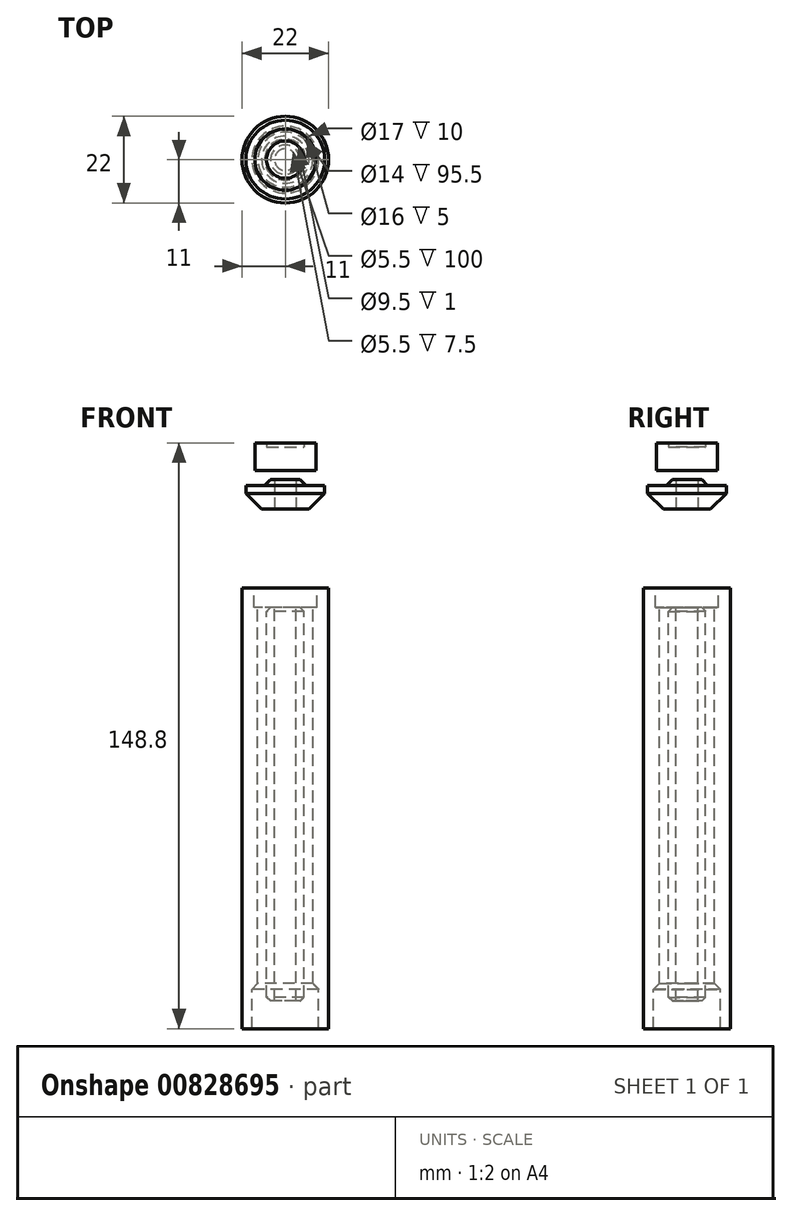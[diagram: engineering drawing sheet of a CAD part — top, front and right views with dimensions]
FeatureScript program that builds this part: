
annotation { "Feature Type Name" : "Feature", "Feature Type Description" : "" }
export const myFeature = defineFeature(function(context is Context, id is Id, definition is map)
    precondition{}
    {
        {
            var Q0;
            Q0=qCreatedBy(makeId("Front.planeOp"),FACE);
            var sketch = newSketch(context, id + "F0", { "sketchPlane" : qUnion([Q0])});
            skLineSegment(sketch, "E0", {"start": v(0, 0) * mm, "end": v(0, 15.44) * mm, "construction": true});
            skLineSegment(sketch, "E1", {"start": v(-2.75, 0) * mm, "end": v(-2.75, 6) * mm});
            skLineSegment(sketch, "E2", {"start": v(-2.75, 6) * mm, "end": v(-10, 6) * mm});
            skLineSegment(sketch, "E3", {"start": v(-10, 6) * mm, "end": v(-10, 4) * mm});
            skLineSegment(sketch, "E4", {"start": v(-10, 4) * mm, "end": v(-6, 0) * mm});
            skLineSegment(sketch, "E5", {"start": v(-6, 0) * mm, "end": v(-2.75, 0) * mm});
            skLineSegment(sketch, "E6.bottom", {"start": v(-2.75, 6) * mm, "end": v(-3.75, 6) * mm});
            skLineSegment(sketch, "E6.top", {"start": v(-2.75, 7.5) * mm, "end": v(-3.75, 7.5) * mm});
            skLineSegment(sketch, "E6.left", {"start": v(-2.75, 6) * mm, "end": v(-2.75, 7.5) * mm});
            skLineSegment(sketch, "E6.right", {"start": v(-3.75, 6) * mm, "end": v(-3.75, 7.5) * mm});
            skSolve(sketch);
        }
        {
            var Q0;
            {var subQ2=sQuery(id+"F0.wireOp",EDGE,"E1");Q0=qUnion([makeQuery(id+"F0.imprint","IMPRINT",FACE,{"disambiguationData":[TD([[makeQuery(id+"F0.imprint","IMPRINT",EDGE,{"derivedFrom":subQ2}),1.0]])]}),makeQuery(id+"F0.imprint","IMPRINT",FACE,{"disambiguationData":[TD([[makeQuery(id+"F0.imprint","IMPRINT",EDGE,{"derivedFrom":sQuery(id+"F0.wireOp",EDGE,"E6.top")}),1.0]])]})]);}
            var Q1;
            Q1=sQuery(id+"F0.wireOp",EDGE,"E0");
            revolve(context, id + "F1", {"surfaceOperationType" : NewSurfaceOperationType.NEW, "entities" : qUnion([Q0]), "axis" : qUnion([Q1]), "revolveType" : RevolveType.FULL});
        }
        {
            var Q0;
            Q0=qCreatedBy(makeId("Front.planeOp"),FACE);
            var sketch = newSketch(context, id + "F2", { "sketchPlane" : qUnion([Q0])});
            skLineSegment(sketch, "E7", {"start": v(0, 0) * mm, "end": v(0, -20.61) * mm, "construction": true});
            skLineSegment(sketch, "E8.bottom", {"start": v(-2.75, -125) * mm, "end": v(-3.75, -125) * mm});
            skLineSegment(sketch, "E8.top", {"start": v(-2.75, -25) * mm, "end": v(-3.75, -25) * mm});
            skLineSegment(sketch, "E8.left", {"start": v(-2.75, -125) * mm, "end": v(-2.75, -25) * mm});
            skLineSegment(sketch, "E8.right", {"start": v(-3.75, -125) * mm, "end": v(-3.75, -25) * mm});
            skLineSegment(sketch, "E9", {"start": v(-3.75, -25) * mm, "end": v(-4.75, -26) * mm});
            skLineSegment(sketch, "E10", {"start": v(-4.75, -26) * mm, "end": v(-4.75, -124) * mm});
            skLineSegment(sketch, "E11", {"start": v(-4.75, -124) * mm, "end": v(-3.75, -125) * mm});
            skLineSegment(sketch, "E12", {"start": v(-2.75, -75) * mm, "end": v(-4.37, -75) * mm, "construction": true});
            skSolve(sketch);
        }
        {
            var Q0;
            Q0 = qSketchRegion(id + "F2", true);
            var Q1;
            Q1=sQuery(id+"F2.wireOp",EDGE,"E7");
            revolve(context, id + "F3", {"surfaceOperationType" : NewSurfaceOperationType.NEW, "entities" : qUnion([Q0]), "axis" : qUnion([Q1]), "revolveType" : RevolveType.FULL});
        }
        {
            var Q0;
            Q0=qCreatedBy(makeId("Front.planeOp"),FACE);
            var sketch = newSketch(context, id + "F4", { "sketchPlane" : qUnion([Q0])});
            skLineSegment(sketch, "E13", {"start": v(-11, -20) * mm, "end": v(-11, -132) * mm});
            skLineSegment(sketch, "E14", {"start": v(-11, -132) * mm, "end": v(-8.5, -132) * mm});
            skLineSegment(sketch, "E15", {"start": v(-8.5, -132) * mm, "end": v(-8.5, -122) * mm});
            skLineSegment(sketch, "E16", {"start": v(-8.5, -122) * mm, "end": v(-7, -120.5) * mm});
            skLineSegment(sketch, "E17", {"start": v(-7, -120.5) * mm, "end": v(-7, -25) * mm});
            skLineSegment(sketch, "E18", {"start": v(-7, -25) * mm, "end": v(-8, -25) * mm});
            skLineSegment(sketch, "E19", {"start": v(-8, -25) * mm, "end": v(-8, -20) * mm});
            skLineSegment(sketch, "E20", {"start": v(-8, -20) * mm, "end": v(-11, -20) * mm});
            skLineSegment(sketch, "E21", {"start": v(0, 0) * mm, "end": v(0, -267.75) * mm, "construction": true});
            skSolve(sketch);
        }
        {
            var Q0;
            Q0 = qSketchRegion(id + "F4", true);
            var Q1;
            Q1=sQuery(id+"F4.wireOp",EDGE,"E21");
            revolve(context, id + "F5", {"surfaceOperationType" : NewSurfaceOperationType.NEW, "entities" : qUnion([Q0]), "axis" : qUnion([Q1]), "revolveType" : RevolveType.FULL});
        }
        {
            var Q0;
            Q0=makeQuery(id+"F1.opRevolve","SWEPT_EDGE",EDGE,{"disambiguationData":[OSD([sQuery(id+"F0.wireOp",EDGE,"E2"),sQuery(id+"F0.wireOp",EDGE,"E6.right")])]});
            chamfer(context, id + "F6", {"entities" : qUnion([Q0]), "width" : 1.5 * mm, "tangentPropagation" : true});
        }
        {
            var Q0;
            Q0=qCreatedBy(makeId("Front.planeOp"),FACE);
            var sketch = newSketch(context, id + "F7", { "sketchPlane" : qUnion([Q0])});
            skLineSegment(sketch, "E22", {"start": v(0, 0) * mm, "end": v(0, 18) * mm, "construction": true});
            skLineSegment(sketch, "E23.bottom", {"start": v(0, 9.8) * mm, "end": v(-7.75, 9.8) * mm});
            skLineSegment(sketch, "E23.top", {"start": v(0, 15.8) * mm, "end": v(-7.75, 15.8) * mm});
            skLineSegment(sketch, "E23.left", {"start": v(0, 9.8) * mm, "end": v(0, 15.8) * mm});
            skLineSegment(sketch, "E23.right", {"start": v(-7.75, 9.8) * mm, "end": v(-7.75, 15.8) * mm});
            skLineSegment(sketch, "E24.bottom", {"start": v(-7.75, 15.8) * mm, "end": v(-4.75, 15.8) * mm});
            skLineSegment(sketch, "E24.top", {"start": v(-7.75, 16.8) * mm, "end": v(-4.75, 16.8) * mm});
            skLineSegment(sketch, "E24.left", {"start": v(-7.75, 15.8) * mm, "end": v(-7.75, 16.8) * mm});
            skLineSegment(sketch, "E24.right", {"start": v(-4.75, 15.8) * mm, "end": v(-4.75, 16.8) * mm});
            skSolve(sketch);
        }
        {
            var Q0;
            Q0=makeQuery(id+"F7.imprint","IMPRINT",FACE,{"disambiguationData":[TD([[makeQuery(id+"F7.imprint","IMPRINT",EDGE,{"derivedFrom":sQuery(id+"F7.wireOp",EDGE,"E24.top")}),-1.0]])]});
            var Q1;
            Q1=makeQuery(id+"F7.imprint","IMPRINT",FACE,{"disambiguationData":[TD([[makeQuery(id+"F7.imprint","IMPRINT",EDGE,{"derivedFrom":sQuery(id+"F7.wireOp",EDGE,"E23.bottom")}),-1.0]])]});
            var Q2;
            Q2=sQuery(id+"F7.wireOp",EDGE,"E22");
            revolve(context, id + "F8", {"surfaceOperationType" : NewSurfaceOperationType.NEW, "entities" : qUnion([Q0, Q1]), "axis" : qUnion([Q2]), "revolveType" : RevolveType.FULL});
        }
    });
